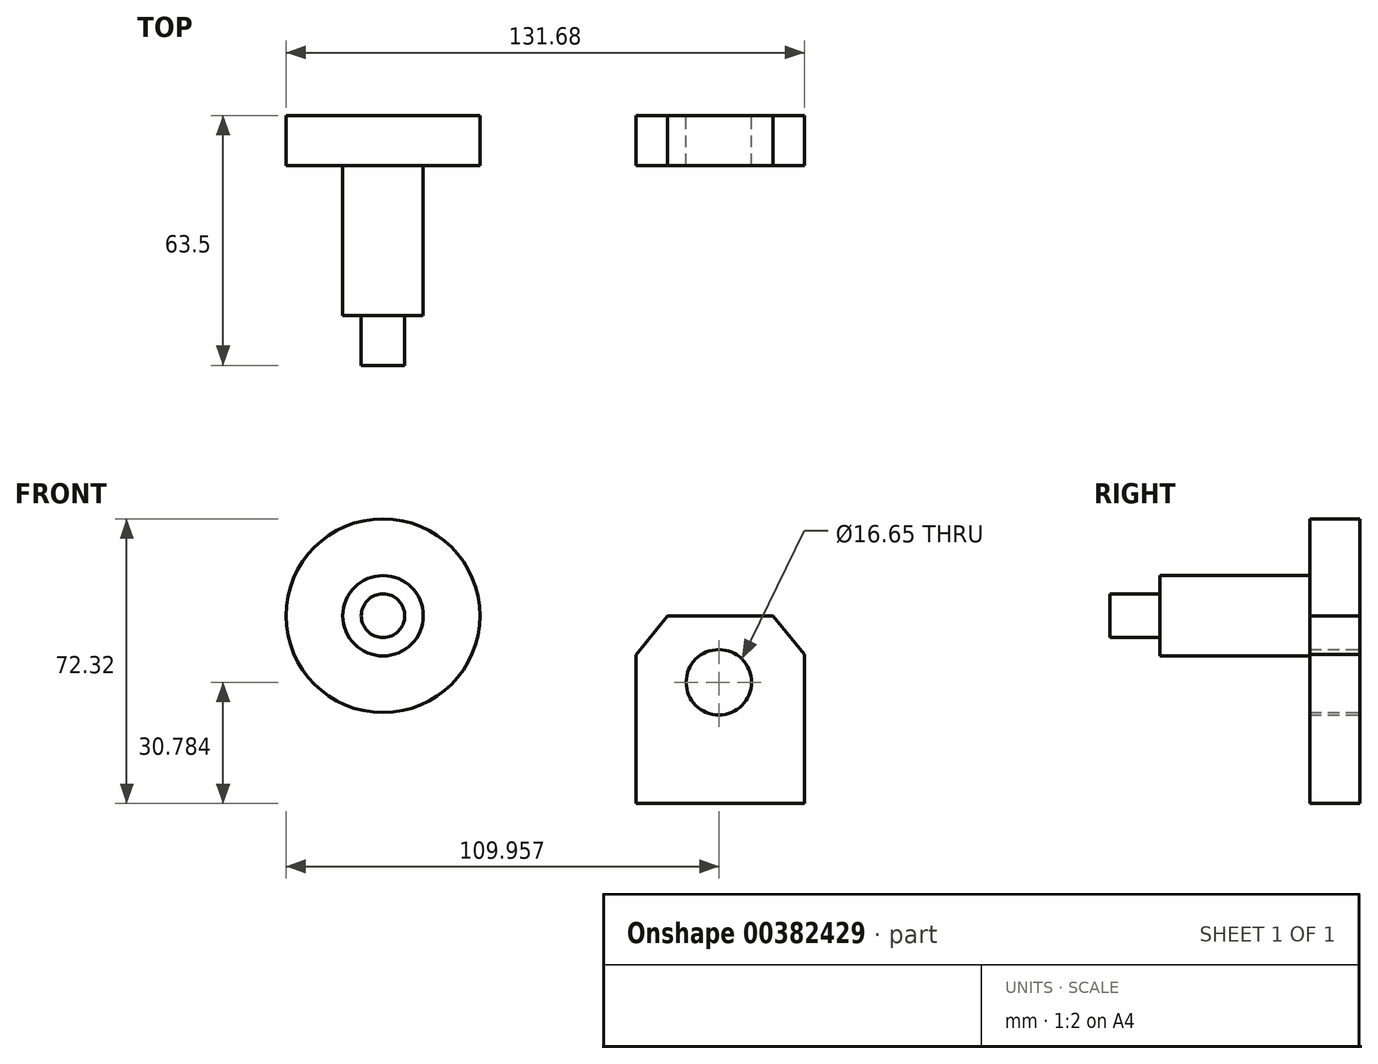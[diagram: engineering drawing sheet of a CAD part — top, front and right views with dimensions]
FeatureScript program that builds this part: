
annotation { "Feature Type Name" : "Feature", "Feature Type Description" : "" }
export const myFeature = defineFeature(function(context is Context, id is Id, definition is map)
    precondition{}
    {
        {
            var Q0;
            Q0=qCreatedBy(makeId("Front.planeOp"),FACE);
            var sketch = newSketch(context, id + "F0", { "sketchPlane" : qUnion([Q0])});
            skLineSegment(sketch, "E0", {"start": v(29.26, 0) * mm, "end": v(56.08, 0) * mm});
            skLineSegment(sketch, "E1", {"start": v(56.08, 0) * mm, "end": v(64.09, -9.84) * mm});
            skLineSegment(sketch, "E2", {"start": v(29.26, 0) * mm, "end": v(21.34, -9.9) * mm});
            skLineSegment(sketch, "E3", {"start": v(21.34, -9.9) * mm, "end": v(21.34, -47.7) * mm});
            skLineSegment(sketch, "E4", {"start": v(64.09, -9.84) * mm, "end": v(64.09, -47.64) * mm});
            skLineSegment(sketch, "E5", {"start": v(64.09, -47.64) * mm, "end": v(21.34, -47.7) * mm});
            skCircle(sketch, "E6", {"center": v(42.37, -16.92) * mm, "radius": 8.33 * mm});
            skSolve(sketch);
        }
        {
            var Q0;
            Q0 = qSketchRegion(id + "F0", true);
            extrude(context, id + "F1", {"entities" : qUnion([Q0]), "depth" : 12.7 * mm});
        }
        {
            var Q0;
            Q0=qCreatedBy(makeId("Front.planeOp"),FACE);
            var sketch = newSketch(context, id + "F2", { "sketchPlane" : qUnion([Q0])});
            skCircle(sketch, "E7", {"center": v(-42.98, 0) * mm, "radius": 24.62 * mm});
            skCircle(sketch, "E8", {"center": v(-42.98, 0) * mm, "radius": 10.22 * mm});
            skCircle(sketch, "E9", {"center": v(-42.98, 0) * mm, "radius": 5.53 * mm});
            skSolve(sketch);
        }
        {
            var Q0;
            Q0=makeQuery(id+"F2.imprint","IMPRINT",FACE,{"disambiguationData":[TD([[makeQuery(id+"F2.imprint","IMPRINT",EDGE,{"derivedFrom":sQuery(id+"F2.wireOp",EDGE,"E8")}),1.0]])]});
            extrude(context, id + "F3", {"entities" : qUnion([Q0]), "depth" : 50.8 * mm});
        }
        {
            var Q0;
            Q0=makeQuery(id+"F2.imprint","IMPRINT",FACE,{"disambiguationData":[TD([[makeQuery(id+"F2.imprint","IMPRINT",EDGE,{"derivedFrom":sQuery(id+"F2.wireOp",EDGE,"E7")}),1.0]])]});
            extrude(context, id + "F4", {"entities" : qUnion([Q0]), "operationType" : NewBodyOperationType.ADD, "depth" : 12.7 * mm});
        }
        {
            var Q0;
            Q0=makeQuery(id+"F2.imprint","IMPRINT",FACE,{"disambiguationData":[TD([[makeQuery(id+"F2.imprint","IMPRINT",EDGE,{"derivedFrom":sQuery(id+"F2.wireOp",EDGE,"E9")}),1.0]])]});
            extrude(context, id + "F5", {"entities" : qUnion([Q0]), "operationType" : NewBodyOperationType.ADD, "depth" : 63.5 * mm});
        }
    });
